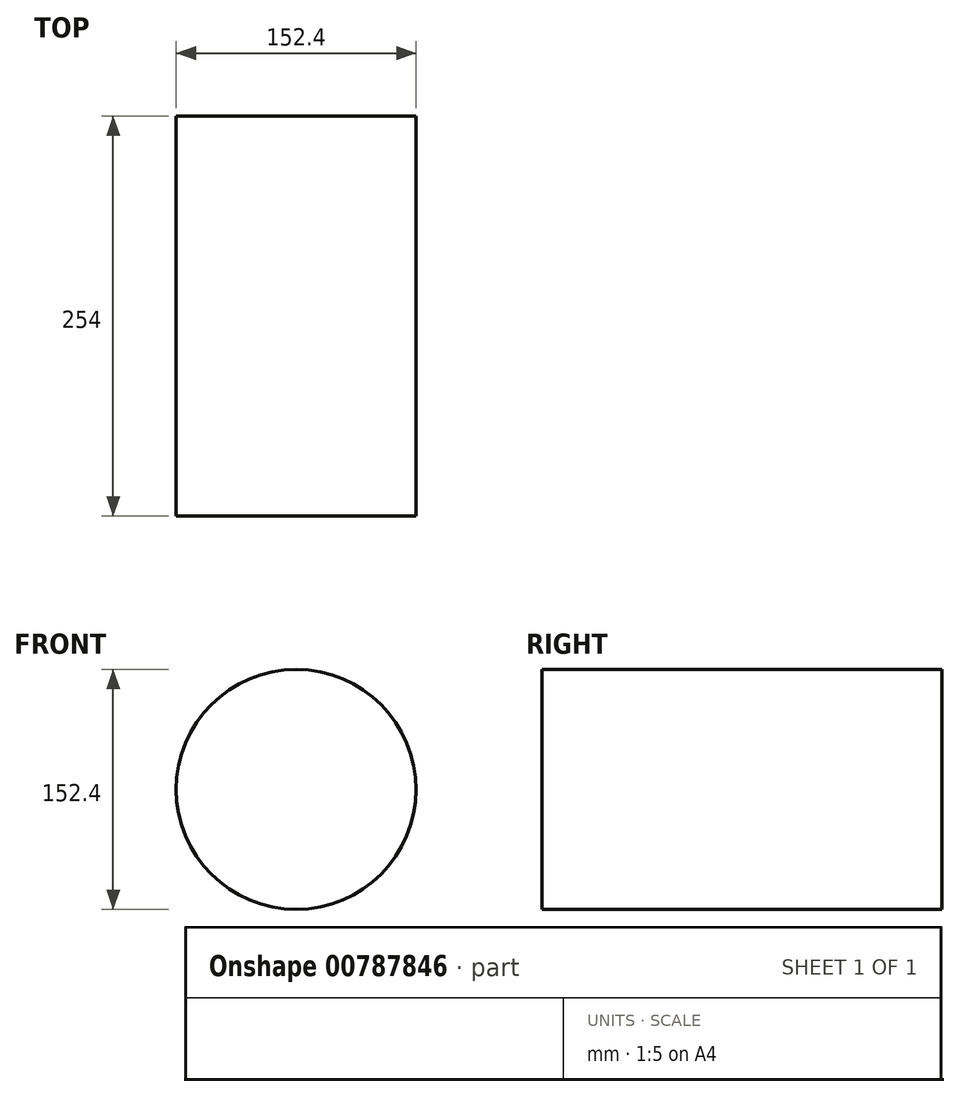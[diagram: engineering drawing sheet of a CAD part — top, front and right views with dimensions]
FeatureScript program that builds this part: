
annotation { "Feature Type Name" : "Feature", "Feature Type Description" : "" }
export const myFeature = defineFeature(function(context is Context, id is Id, definition is map)
    precondition{}
    {
        {
            var Q0;
            Q0=qCreatedBy(makeId("Right.planeOp"),FACE);
            var sketch = newSketch(context, id + "F0", { "sketchPlane" : qUnion([Q0])});
            skLineSegment(sketch, "E0.bottom", {"start": v(0, 0) * mm, "end": v(254, 0) * mm});
            skLineSegment(sketch, "E0.top", {"start": v(0, 76.2) * mm, "end": v(254, 76.2) * mm});
            skLineSegment(sketch, "E0.left", {"start": v(0, 0) * mm, "end": v(0, 76.2) * mm});
            skLineSegment(sketch, "E0.right", {"start": v(254, 0) * mm, "end": v(254, 76.2) * mm});
            skLineSegment(sketch, "E1", {"start": v(0, 0) * mm, "end": v(-56.08, 0) * mm});
            skSolve(sketch);
        }
        {
            var Q0;
            Q0=makeQuery(id+"F0.imprint","IMPRINT",FACE,{"disambiguationData":[TD([[makeQuery(id+"F0.imprint","IMPRINT",EDGE,{"derivedFrom":sQuery(id+"F0.wireOp",EDGE,"E0.bottom")}),1.0]])]});
            var Q1;
            Q1=sQuery(id+"F0.wireOp",EDGE,"E1");
            revolve(context, id + "F1", {"surfaceOperationType" : NewSurfaceOperationType.NEW, "entities" : qUnion([Q0]), "axis" : qUnion([Q1]), "revolveType" : RevolveType.FULL});
        }
    });
